# Revit family: Haworth_Atwell_Table_Freestanding
name_source: partatom
category: Furniture
revit_build: Autodesk Revit 2018 (Build: 20170223_1515(x64)
units: mm (PartAtom-declared; Revit-internal decimal feet)

## family parameters
Always vertical = Yes
Cut with Voids When Loaded = No
OmniClass Number = 23.40.20.00
OmniClass Title = General Furniture and Specialties
Room Calculation Point = No
Shared = No
Work Plane-Based = No

## types (2) — shared parameters
Actual Depth = 1' - 9"
Actual Height = 1' - 5 1/2"
Assembly Code = E2020200
Manufacturer = Haworth
Model = Haworth Atwell
Size = Verify Final Dim. w/ Haworth
Sustainability Info = https://www.haworth.com
URL = http://healthcare.haworth.com
URL - Product = http://healthcare.haworth.com
Version = 0
Warranty = https://healthcare.haworth.com

## per-type parameters (varying)
| type | Actual Width | Coffee Table | Description | End Table |
| HE900-FE - 21w | 1' - 9" | No | Free Standing End Table | Yes |
| HE900-FC - 48w | 4' - 0" | Yes | Free Standing Coffee Table | No |

## geometry (parser evidence)
native form markers: Sweep x3
no freeform markers — native parametric forms only
